# Revit family: Shower-Valve_Trim-KOHLER-July-K-16316IN-1
name_source: partatom
category: Plumbing Fixtures
units: mm (PartAtom-declared; Revit-internal decimal feet)

## family parameters
Cut with Voids When Loaded = No
Host = Face
OmniClass Number = 23.31.17.00
OmniClass Title = Showers
Part Type = Normal
Room Calculation Point = No
Round Connector Dimension = Use Diameter
Shared = No

## types (4) — shared parameters
ADA Compliant = No
Assembly Code = D2010700
CW Connection = Yes
Cold Water Inlet = Cold Water Inlet
Date Modified = 05/22/2024
Default Elevation = 72"
Description = Recessed bath and shower faucet trim with lever handle and diverter button in polished chrome
Drain Included = No
Flow Rate = 0 GPM
HW Connection = Yes
Handle Clearance = 3 13/16"
Height = 6 9/16"
Hot Water Inlet = Hot Water Inlet
Length = 2 7/8"
Manufacturer = Kohler Co.
Master Format 2014 = 22 42 23
Master Format 2014 Name = Residential Showers
Material = Premium Metal Construction
Pressure = 0.00 psi
Product Documentation Link = https://techcomm.kohler.com
Product Name = July
URL = https://www.kohler.co.in
Vent Connection = No
Waste Connection = No
Waste Water Outlet = Waste Water Outlet
WaterSense Certified = No
Width = 4 7/16"

## per-type parameters (varying)
| type | Finish | Model | Product Page URL | Type |
| AF-Vibrant French Gold | Kohler-Metal-AF-Vibrant_French_Gold | K-16316IN-4FP-CP | https://www.kohler.co.in | 1 |
| BN-Vibrant Brushed Nickel | Kohler-Metal-BN-Vibrant_Brushed_Nickel | K-16316IN-4FP-AF |  | 2 |
| CP-Polished Chrome | Kohler-Metal-CP-Polished_Chrome | K-16316IN-4FP-BN |  | 3 |
| PGD-Modern Polished Gold | Kohler-Metal-PGD-Modern_Polished_Gold | K-16316IN-4FP-PGD |  | 4 |

## geometry (parser evidence)
native form markers: Sweep x4
no freeform markers — native parametric forms only
